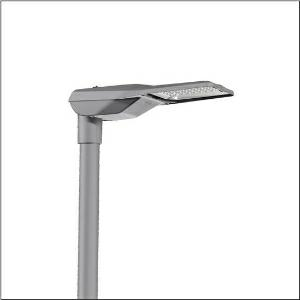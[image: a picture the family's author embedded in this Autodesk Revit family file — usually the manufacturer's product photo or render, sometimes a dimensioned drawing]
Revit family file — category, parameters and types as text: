
# Revit family: streetlight_sl_21_iq_mini___st1_0ab_5xe2m31v08hb_1211
name_source: partatom
category: Lighting Fixtures
units: mm (PartAtom-declared; Revit-internal decimal feet)

## family parameters
Cut with Voids When Loaded = No
Host = Face
Light Source = No
Part Type = Normal
Room Calculation Point = No
Round Connector Dimension = Use Diameter
Shared = No

## types (1)
- --- (1 x LED, 8580 lm, 71 W, 3000K)
    Apparent Load = 71 VA
    CIE Flux Codes = 38 73 97 100 100
    Color Rendering = 70
    Color Temperature = 3000K
    Default Elevation = 1800 mm
    Description = Streetlight SL 21 iQ mini, mast luminaire, primary light control with lens, of PMMA, primary optical cover: cover, of toughened safety glass, transparent, light distribution: ST1.0aB, light emission: direct distribution, primary light characteristic: asymmetric, installation type: post-top, side-entry, LED, High Power LED, rated luminous flux: 8.580lm, luminous efficacy: 121lm/W, light colour: 730, colour temperature: 3000K, control gear: iQ-Street Remote, D4i with power reduction, control: pre-setting: logarithmic dimming characteristic, Street-Remote, Auto-Match, Temp-Guard, Lumen-Switch, Night-Set, Smart-Wire, Light-Fading, Desk-Remote (wireless, voltage-free reading and setting of iQ features in the workshop via application-optimized NFC function/RFID function), optimised constant luminous flux control (CLO 2.0), mains connection: 220..240V, AC, 50/60Hz, start of lifetime: 71W, end of service life: 75W, reduction: 30W, luminaire housing, of diecast aluminium, powder-coated, SITECO metallic grey (DB 702S), corrosivity category C5 high according to DIN EN ISO 12944, please order mast flange separately, inclination adjustable: 0°, 5°, 10°, 15°, sealing non-destructively replaceable, multi-level sealing system, length: 628mm, width: 235mm, height: 110mm, mast flange for spigot size: 42mm (side-entry): 5XC10008XM4, 60/48mm (side-entry/post-top): 5XC10108XM2, 76/60mm (side-entry/post-top): 5XC10108XM1, mounting height: 4..8m, Smart Interface above, protection rating (complete): IP66, insulation class (complete): insulation class II (safety insulation), certification: CE, ENEC, ENEC+, VDE, impact resistance: IK10, permissible operating ambient temperature for outdoor applications: -40..+50°C, standard-compliant lighting for roads and squares, packaging unit: 1 piece

Light Distribution: ST1.0aB
    Height = 110 mm
    Lamp = 1 x LED
    Lamp Light Flux = 8580 lm
    Lamp Power = 71 W
    Lamp count = 1
    Length = 625 mm
    Luminous efficacy = 121 lm/W
    Manufacturer = Siteco
    ModVariant = No
    Model = 5XE2M31V08HB
    Number of Poles = 1
    OnlyDefault = Yes
    Power Factor = 1
    Product Name = Streetlight SL 21 iQ mini | ST1.0aB
    Product group = mast luminaire | pylon top
    ProductGroupID = 6100
    Protection Class = Protection class II
    Protection Degree = IP 66
    RLX_Detail_Level = 1
    RLX_Emergency_Light_Flux = 0 lm
    RLX_Emergency_Type = 0
    RLX_Emergency_Type_DB = No
    RlxData = <blob elided: 92349 chars, md5=383e6625>
    Socket = socket
    Standby Power = 0 W
    System Light Flux = 8580 lm
    System Power = 71 W
    Type Comments = factory setting: luminous flux: 100 % | dim-lin: 254 | 716 mA
    Type Image = l_1003515.jpg
    URL = http://relux.com
    VarID = @adj_112469
    Voltage = 0 V
    Weight = 0.00 kg
    Width = 234 mm

## geometry (parser evidence)
native form markers: Blend x4, Sweep x11
no freeform markers — native parametric forms only
